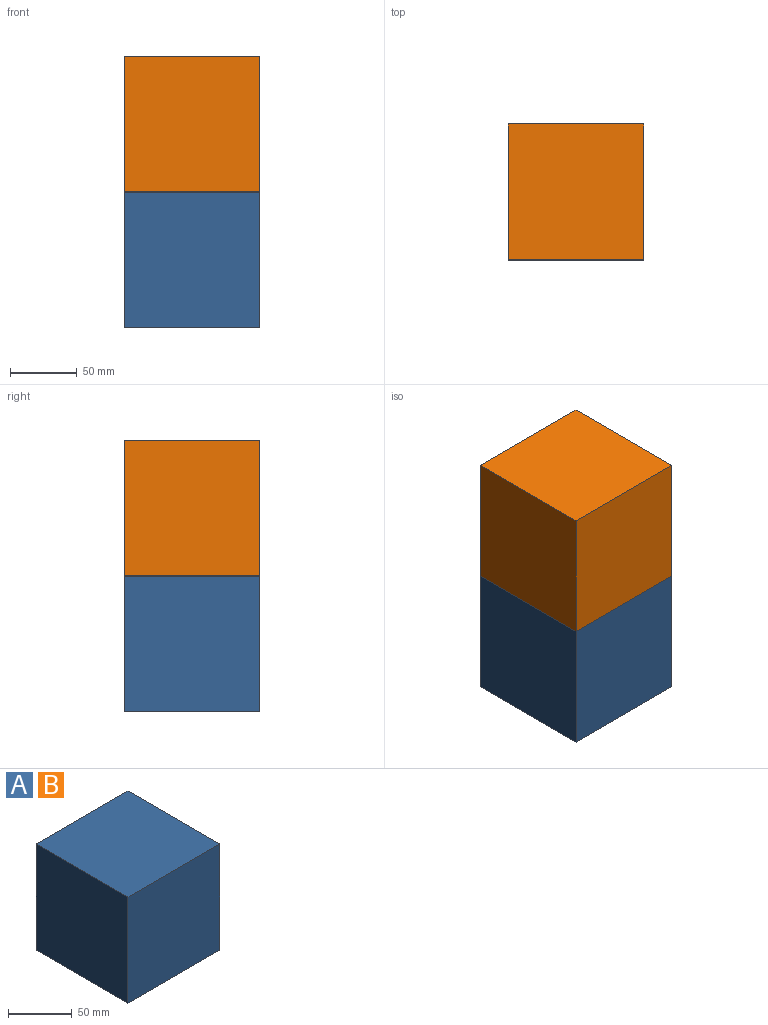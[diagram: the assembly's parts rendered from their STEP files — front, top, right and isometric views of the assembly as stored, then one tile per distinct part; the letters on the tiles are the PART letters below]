
ASSEMBLY  parts=2 mates=1
PART A: 6 faces, bbox 101.6x101.6x101.6 mm
  f0: plane 101.6x101.6mm, normal (1,0,0), area 10322.6mm2, adj f1,f3,f4,f5
  f1: plane 101.6x101.6mm, normal (0,0,1), area 10322.6mm2, adj f0,f2,f4,f5
  f2: plane 101.6x101.6mm, normal (-1,0,0), area 10322.6mm2, adj f1,f3,f4,f5
  f3: plane 101.6x101.6mm, normal (0,0,-1), area 10322.6mm2, adj f0,f2,f4,f5
  f4: plane 101.6x101.6mm, normal (0,-1,0), area 10322.6mm2, adj f0,f1,f2,f3
  f5: plane 101.6x101.6mm, normal (0,1,0), area 10322.6mm2, adj f0,f1,f2,f3
PART B: same geometry as A
PLACE A t=(-219.78,76.47,162.27)mm
PLACE B t=(-219.78,76.47,263.87)mm
MATE fastened A.f1 <-> B.f3  axis (0,0,1) through (-258.35,25.67,211.44)mm
